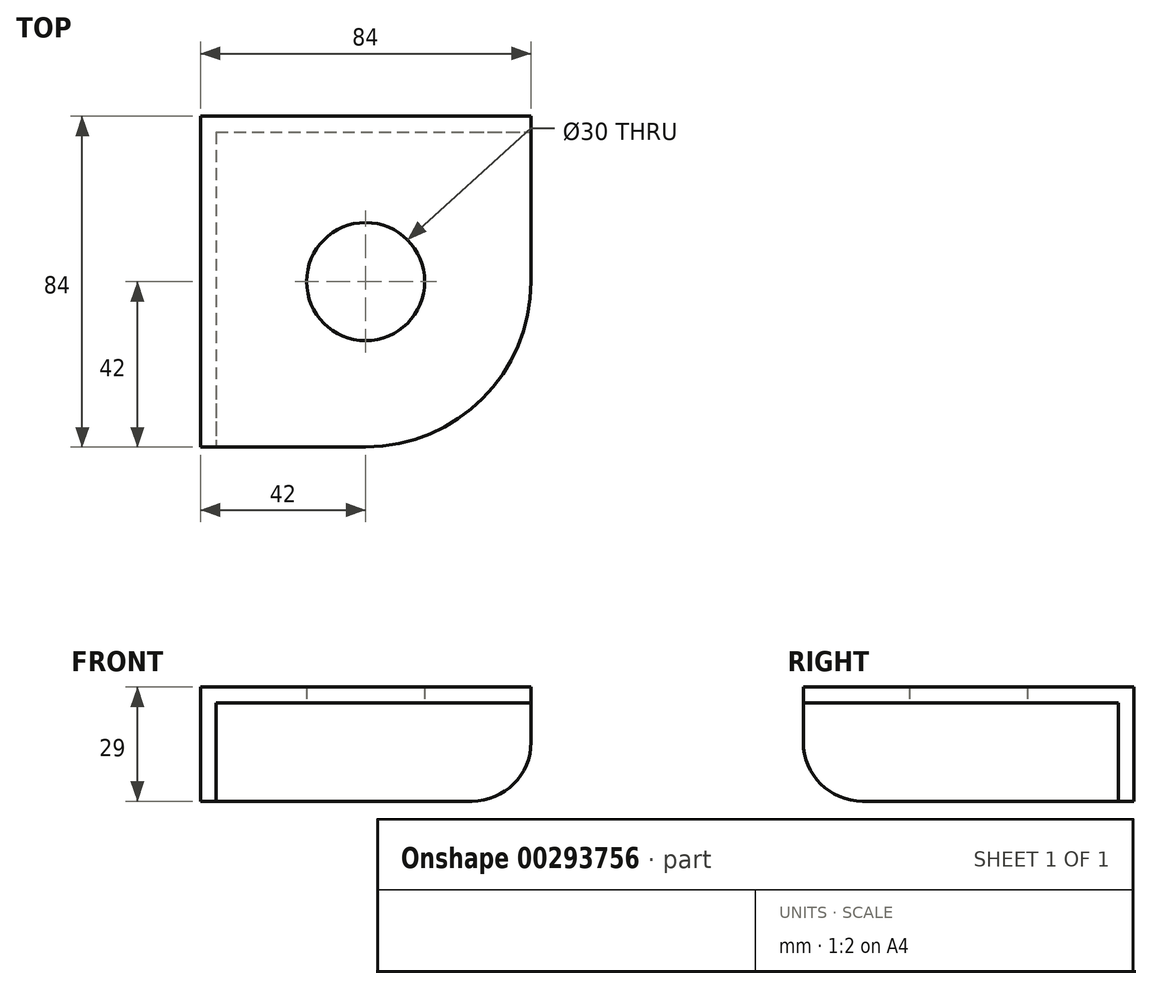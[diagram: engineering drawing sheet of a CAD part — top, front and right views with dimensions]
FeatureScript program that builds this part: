
annotation { "Feature Type Name" : "Feature", "Feature Type Description" : "" }
export const myFeature = defineFeature(function(context is Context, id is Id, definition is map)
    precondition{}
    {
        {
            var Q0;
            Q0=qCreatedBy(makeId("Top.planeOp"),FACE);
            var sketch = newSketch(context, id + "F0", { "sketchPlane" : qUnion([Q0])});
            skLineSegment(sketch, "E0.bottom", {"start": v(0, 0) * mm, "end": v(84, 0) * mm});
            skLineSegment(sketch, "E0.top", {"start": v(0, -84) * mm, "end": v(42, -84) * mm});
            skLineSegment(sketch, "E0.left", {"start": v(0, 0) * mm, "end": v(0, -84) * mm});
            skLineSegment(sketch, "E0.right", {"start": v(84, 0) * mm, "end": v(84, -42) * mm});
            skArc(sketch, "E1", {"start": v(42, -84) * mm, "mid": v(71.7, -71.7) * mm, "end": v(84, -42) * mm});
            skPoint(sketch, "E1.centerSnap0", {"position": v(0, -42) * mm});
            skPoint(sketch, "E1.centerSnap1", {"position": v(42, 0) * mm});
            skCircle(sketch, "E2", {"center": v(42, -42) * mm, "radius": 15 * mm});
            skSolve(sketch);
        }
        {
            var Q0;
            Q0 = qSketchRegion(id + "F0", true);
            extrude(context, id + "F1", {"entities" : qUnion([Q0]), "depth" : 4 * mm});
        }
        {
            var Q0;
            Q0=makeQuery(id+"F1.opExtrude","CAP_FACE",FACE,{"disambiguationData":[OSD([sQuery(id+"F0.wireOp",EDGE,"E0.bottom"),sQuery(id+"F0.wireOp",EDGE,"E0.top"),sQuery(id+"F0.wireOp",EDGE,"E0.left"),sQuery(id+"F0.wireOp",EDGE,"E0.right"),sQuery(id+"F0.wireOp",EDGE,"E1")])],"isStart":true});
            var sketch = newSketch(context, id + "F2", { "sketchPlane" : qUnion([Q0])});
            skLineSegment(sketch, "E3.0", {"start": v(4, 4) * mm, "end": v(4, 84) * mm});
            skLineSegment(sketch, "E3.1", {"start": v(4, 4) * mm, "end": v(84, 4) * mm});
            skSolve(sketch);
        }
        {
            var Q0;
            Q0 = qSketchRegion(id + "F2", true);
            var Q1;
            {var subQ3=sQuery(id+"F2.wireOp",EDGE,"E3.0");Q1=makeQuery(id+"F2.imprint","IMPRINT",FACE,{"disambiguationData":[TD([[makeQuery(id+"F2.imprint","IMPRINT",EDGE,{"derivedFrom":subQ3}),1.0]])]});}
            extrude(context, id + "F3", {"entities" : qUnion([Q0, Q1]), "operationType" : NewBodyOperationType.ADD, "depth" : 25 * mm});
        }
        {
            var Q0;
            Q0=makeQuery(id+"F3.opExtrude","CAP_EDGE",EDGE,{"disambiguationData":[OSD([sQuery(id+"F0.wireOp",EDGE,"E0.top")])],"isStart":false});
            var Q1;
            Q1=makeQuery(id+"F3.opExtrude","CAP_EDGE",EDGE,{"disambiguationData":[OSD([sQuery(id+"F0.wireOp",EDGE,"E0.right")])],"isStart":false});
            fillet(context, id + "F4", {"entities" : qUnion([Q0, Q1]), "radius" : 15 * mm, "tangentPropagation" : true, "allowEdgeOverflow" : false});
        }
    });
